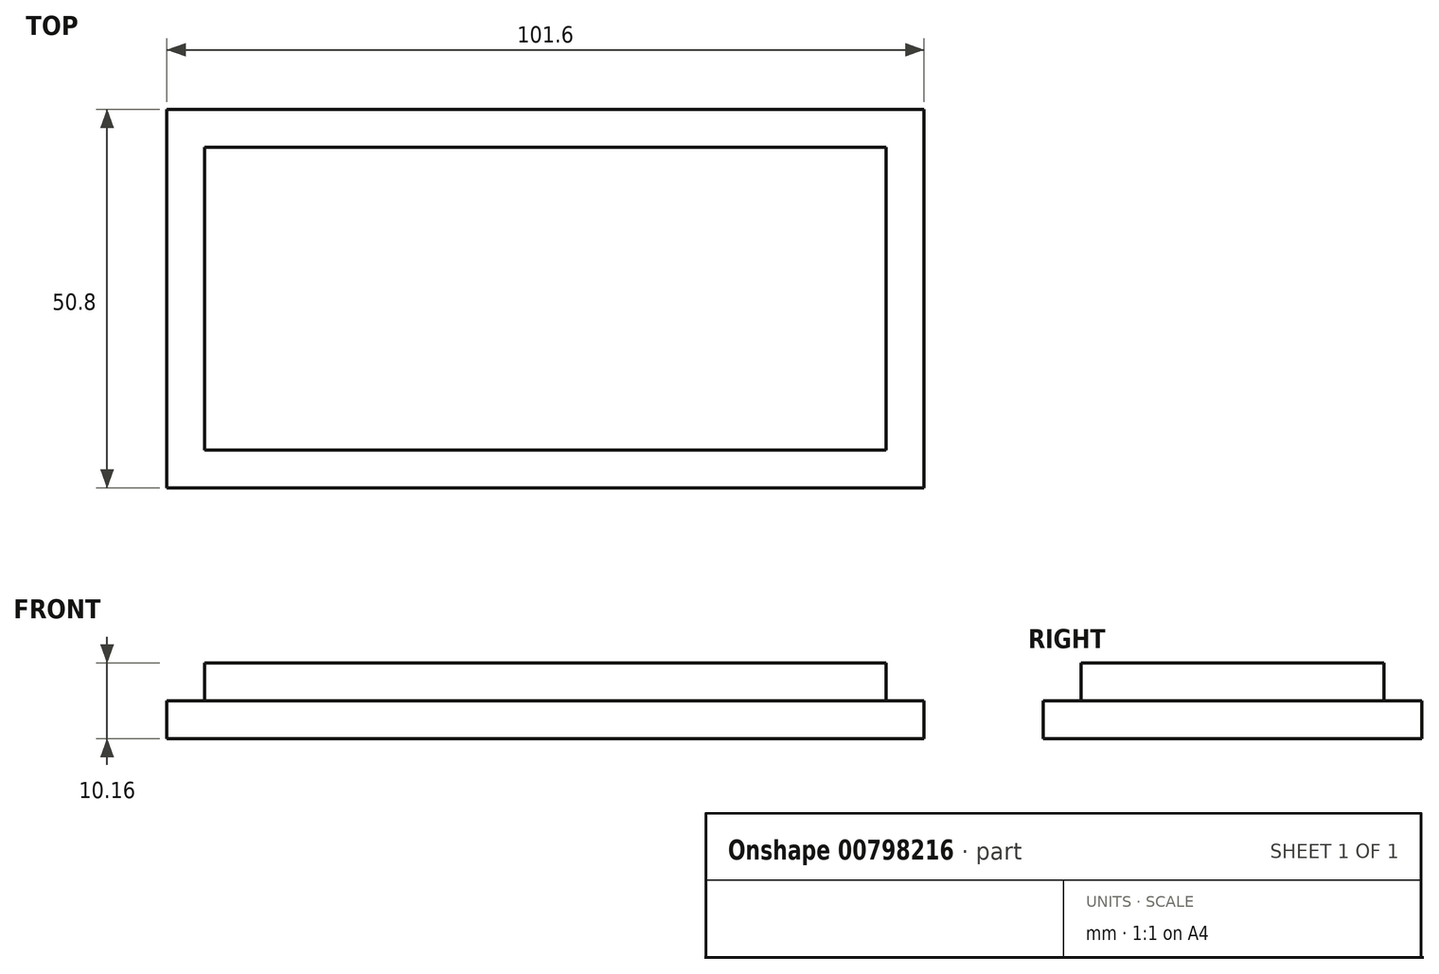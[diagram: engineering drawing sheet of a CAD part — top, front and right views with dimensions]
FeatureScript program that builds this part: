
annotation { "Feature Type Name" : "Feature", "Feature Type Description" : "" }
export const myFeature = defineFeature(function(context is Context, id is Id, definition is map)
    precondition{}
    {
        {
            var Q0;
            Q0=qCreatedBy(makeId("Top.planeOp"),FACE);
            var sketch = newSketch(context, id + "F0", { "sketchPlane" : qUnion([Q0])});
            skLineSegment(sketch, "E0.bottom", {"start": v(-50.8, 25.4) * mm, "end": v(50.8, 25.4) * mm});
            skLineSegment(sketch, "E0.top", {"start": v(-50.8, -25.4) * mm, "end": v(50.8, -25.4) * mm});
            skLineSegment(sketch, "E0.left", {"start": v(-50.8, 25.4) * mm, "end": v(-50.8, -25.4) * mm});
            skLineSegment(sketch, "E0.right", {"start": v(50.8, 25.4) * mm, "end": v(50.8, -25.4) * mm});
            skLineSegment(sketch, "E1.bottom", {"start": v(-45.72, 20.32) * mm, "end": v(45.72, 20.32) * mm});
            skLineSegment(sketch, "E1.top", {"start": v(-45.72, -20.32) * mm, "end": v(45.72, -20.32) * mm});
            skLineSegment(sketch, "E1.left", {"start": v(-45.72, 20.32) * mm, "end": v(-45.72, -20.32) * mm});
            skLineSegment(sketch, "E1.right", {"start": v(45.72, 20.32) * mm, "end": v(45.72, -20.32) * mm});
            skSolve(sketch);
        }
        {
            var Q0;
            Q0=makeQuery(id+"F0.imprint","IMPRINT",FACE,{"disambiguationData":[TD([[makeQuery(id+"F0.imprint","IMPRINT",EDGE,{"derivedFrom":sQuery(id+"F0.wireOp",EDGE,"E1.bottom")}),-1.0]])]});
            extrude(context, id + "F1", {"entities" : qUnion([Q0]), "depth" : 5.08 * mm, "offsetDistance" : 25.4 * mm});
        }
        {
            var Q0;
            Q0 = qSketchRegion(id + "F0", true);
            extrude(context, id + "F2", {"entities" : qUnion([Q0]), "operationType" : NewBodyOperationType.ADD, "depth" : 5.08 * mm, "offsetDistance" : 25.4 * mm});
        }
        {
            var Q0;
            Q0=makeQuery(id+"F0.imprint","IMPRINT",FACE,{"disambiguationData":[TD([[makeQuery(id+"F0.imprint","IMPRINT",EDGE,{"derivedFrom":sQuery(id+"F0.wireOp",EDGE,"E1.bottom")}),-1.0]])]});
            extrude(context, id + "F3", {"entities" : qUnion([Q0]), "operationType" : NewBodyOperationType.ADD, "depth" : 10.16 * mm, "offsetDistance" : 25.4 * mm});
        }
    });
